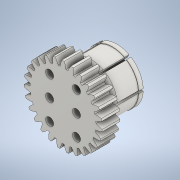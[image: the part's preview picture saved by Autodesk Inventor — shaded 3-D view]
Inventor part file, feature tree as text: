
AUTODESK INVENTOR PART (.ipt)
format: ipt  version: 2022 (Build 260153000, 153)  size: 785,408 bytes
history: native  units: mm (DEFAULTED — no unit token found)
features: sketch x9, extrude x7, fillet x4, plane x3, other x3, pattern_circular x2, revolve x1, projected_geometry x1
ambient origin geometry x8: Origin, YZ Plane, XZ Plane, XY Plane, X Axis, Y Axis, Z Axis, Center Point
bodies: Solid1 (feature_tree)
feature tree (30):
  extrude  "Extrusion1"  Depth=6.0mm TaperAngle=0.0deg
  plane  "Work Plane2"
  plane  "Work Plane8"
  plane  "Work Plane9"
  other  "Цилиндрическое зубчатое зацепление"
  extrude  "Выдавливание5"  Depth=10.0mm TaperAngle=0.0deg
  extrude  "Выдавливание7"  Depth=0.3mm
  extrude  "Выдавливание8"  Depth=0.3mm TaperAngle=0.0deg
  revolve  "Вращение1"
  extrude  "Выдавливание9"  TaperAngle=0.0deg  [1 undecoded]
  extrude  "Выдавливание11"  TaperAngle=0.0deg  [1 undecoded]
  fillet  "Сопряжение4"  Radius=40.825mm
  pattern_circular  "Круговой массив2"  [2 undecoded]
  fillet  "Сопряжение5"  [1 undecoded]
  extrude  "Выдавливание10"  Depth=0.3mm TaperAngle=0.0deg
  fillet  "Сопряжение2"  Radius=15.0mm
  pattern_circular  "Круговой массив1"  [2 undecoded]
  fillet  "Сопряжение3"  Radius=4.5mm
  sketch  "Sketch1"  dims[d0=43.480844mm d1=6.0mm d2=0.0mm]
  sketch  "Sketch2"  dims[d3=40.5mm d4=10.0mm d5=0.0mm d16=40.825mm d17=0.0mm d34=1.163553mm d39=0.0mm d41=0.0mm d43=40.825mm d46=40.825mm d47=0.0mm d48=0.0mm d74=4.0mm d75=0.0mm d80=15.0mm d81=23.0mm d82=4.5mm d83=30.0mm d85=11.5mm d86=20.0mm d88=15.0mm d91=8.0mm d92=0.0mm d93=25.4mm d94=2.0mm d95=0.436332mm d96=60.0mm d98=360.0deg d100=20.0mm d101=0.0mm d102=2.5mm d103=0.3mm d104=12.0mm d105=90.0deg d106=21.0mm d107=20.0mm d108=0.0mm d109=0.5mm d110=10.0mm d111=0.0mm d112=1.0mm d113=80.0mm d114=360.0deg d116=0.5mm d117=0.3mm d118=0.872665mm d119=10.0mm d120=0.0mm d121=0.3mm d122=80.0mm d123=360.0deg d125=0.3mm]
  other  "Srf1"
  sketch  "Эскиз6"
  projected_geometry  "Спроецированная петля1"
  sketch  "Эскиз8"
  sketch  "Эскиз9"
  sketch  "Эскиз10"
  sketch  "Эскиз11"
  sketch  "Эскиз12"
  sketch  "Эскиз13"
  other  "Средний диаметр"
note: 7 required parameter values undecoded (feature->parameter linkage not recoverable at this tier; creation-order binding heuristic only, values carry confidence <= 0.55)
